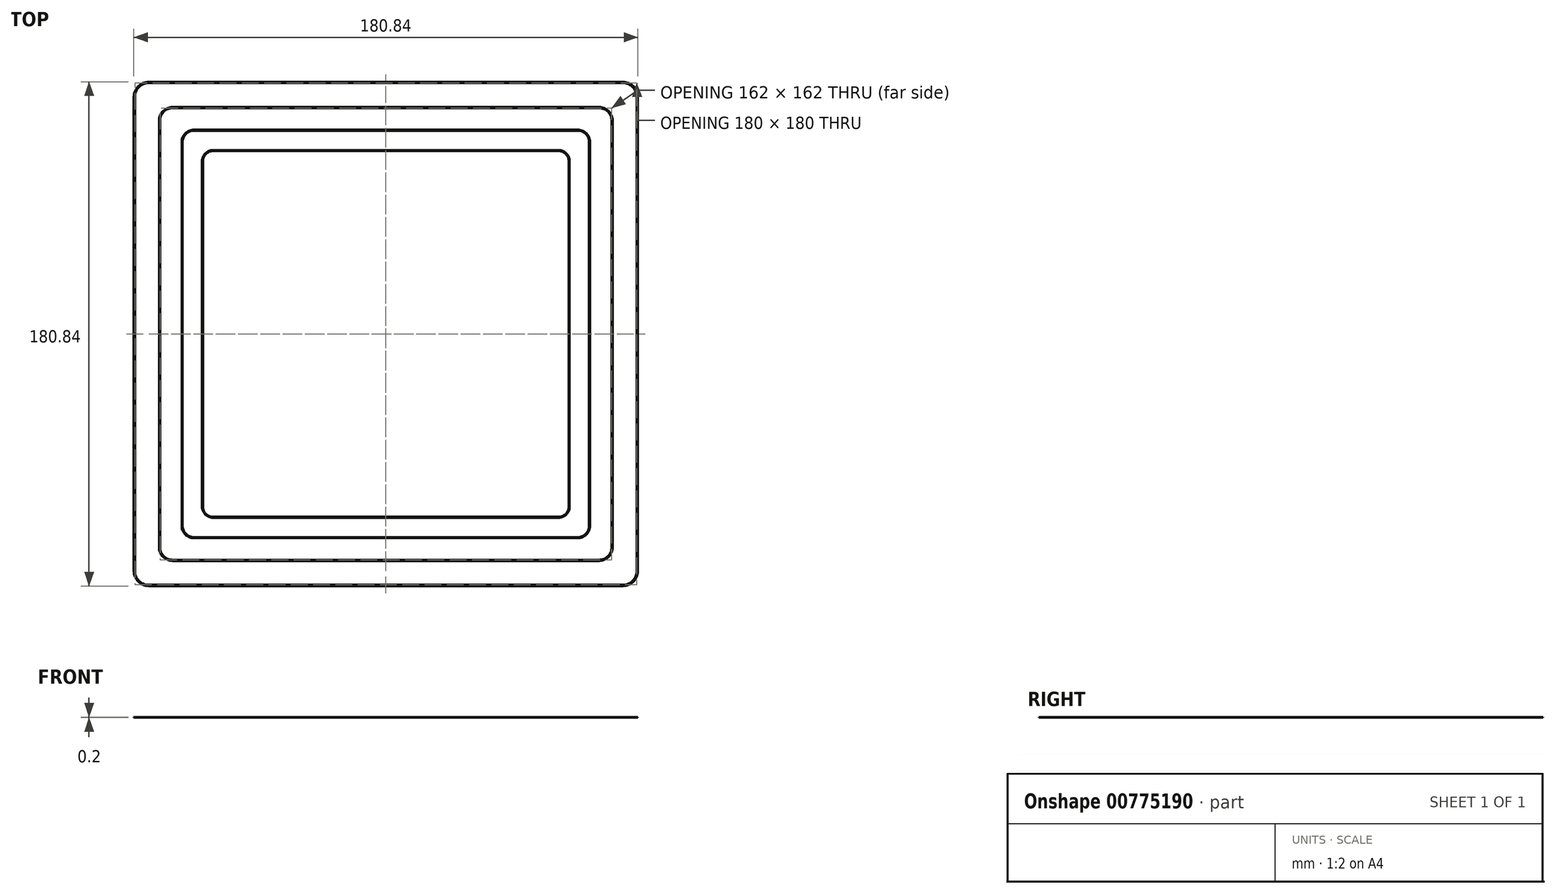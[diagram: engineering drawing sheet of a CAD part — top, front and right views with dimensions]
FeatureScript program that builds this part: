
annotation { "Feature Type Name" : "Feature", "Feature Type Description" : "" }
export const myFeature = defineFeature(function(context is Context, id is Id, definition is map)
    precondition{}
    {
        {
            var Q0;
            Q0=qCreatedBy(makeId("Top.planeOp"),FACE);
            var sketch = newSketch(context, id + "F0", { "sketchPlane" : qUnion([Q0])});
            skLineSegment(sketch, "E0.bottom", {"start": v(85, 90) * mm, "end": v(-85, 90) * mm});
            skLineSegment(sketch, "E0.top", {"start": v(85, -90) * mm, "end": v(-85, -90) * mm});
            skLineSegment(sketch, "E0.left", {"start": v(90, 85) * mm, "end": v(90, -85) * mm});
            skLineSegment(sketch, "E0.right", {"start": v(-90, 85) * mm, "end": v(-90, -85) * mm});
            skPoint(sketch, "E0.middle", {"position": v(0, 0) * mm});
            skPoint(sketch, "E1.visualSharp", {"position": v(-90, 90) * mm});
            skArc(sketch, "E1.filletArc", {"start": v(-85, 90) * mm, "mid": v(-88.54, 88.54) * mm, "end": v(-90, 85) * mm});
            skPoint(sketch, "E2.visualSharp", {"position": v(90, 90) * mm});
            skArc(sketch, "E2.filletArc", {"start": v(90, 85) * mm, "mid": v(88.54, 88.54) * mm, "end": v(85, 90) * mm});
            skPoint(sketch, "E3.visualSharp", {"position": v(90, -90) * mm});
            skArc(sketch, "E3.filletArc", {"start": v(85, -90) * mm, "mid": v(88.54, -88.54) * mm, "end": v(90, -85) * mm});
            skPoint(sketch, "E4.visualSharp", {"position": v(-90, -90) * mm});
            skArc(sketch, "E4.filletArc", {"start": v(-90, -85) * mm, "mid": v(-88.54, -88.54) * mm, "end": v(-85, -90) * mm});
            skArc(sketch, "E5.0", {"start": v(90.42, 85) * mm, "mid": v(88.83, 88.83) * mm, "end": v(85, 90.42) * mm});
            skLineSegment(sketch, "E5.1", {"start": v(90.42, 85) * mm, "end": v(90.42, -85) * mm});
            skLineSegment(sketch, "E5.2", {"start": v(85, 90.42) * mm, "end": v(-85, 90.42) * mm});
            skArc(sketch, "E5.3", {"start": v(85, -90.42) * mm, "mid": v(88.83, -88.83) * mm, "end": v(90.42, -85) * mm});
            skArc(sketch, "E5.4", {"start": v(-85, 90.42) * mm, "mid": v(-88.83, 88.83) * mm, "end": v(-90.42, 85) * mm});
            skLineSegment(sketch, "E5.5", {"start": v(-90.42, 85) * mm, "end": v(-90.42, -85) * mm});
            skArc(sketch, "E5.6", {"start": v(-90.42, -85) * mm, "mid": v(-88.83, -88.83) * mm, "end": v(-85, -90.42) * mm});
            skLineSegment(sketch, "E5.7", {"start": v(85, -90.42) * mm, "end": v(-85, -90.42) * mm});
            skSolve(sketch);
        }
        {
            var Q0;
            Q0 = qSketchRegion(id + "F0", true);
            extrude(context, id + "F1", {"entities" : qUnion([Q0]), "depth" : 0.2 * mm, "offsetDistance" : 25 * mm});
        }
        {
            var Q0;
            Q0=makeQuery(id+"F1.opExtrude","SWEPT_BODY",BODY,{"disambiguationData":[OSD([sQuery(id+"F0.wireOp",EDGE,"E0.bottom"),sQuery(id+"F0.wireOp",EDGE,"E0.top"),sQuery(id+"F0.wireOp",EDGE,"E0.left"),sQuery(id+"F0.wireOp",EDGE,"E0.right"),sQuery(id+"F0.wireOp",EDGE,"E1.filletArc"),sQuery(id+"F0.wireOp",EDGE,"E2.filletArc"),sQuery(id+"F0.wireOp",EDGE,"E3.filletArc"),sQuery(id+"F0.wireOp",EDGE,"E4.filletArc"),sQuery(id+"F0.wireOp",EDGE,"E5.0"),sQuery(id+"F0.wireOp",EDGE,"E5.1"),sQuery(id+"F0.wireOp",EDGE,"E5.2"),sQuery(id+"F0.wireOp",EDGE,"E5.3"),sQuery(id+"F0.wireOp",EDGE,"E5.4"),sQuery(id+"F0.wireOp",EDGE,"E5.5"),sQuery(id+"F0.wireOp",EDGE,"E5.6"),sQuery(id+"F0.wireOp",EDGE,"E5.7")])]});
            var Q1;
            Q1=qCreatedBy(makeId("Origin.pointOp"),VERTEX);
            transform(context, id + "F2", {"entities" : qUnion([Q0]), "transformType" : TransformType.SCALE_UNIFORMLY, "scale" : 0.9, "scalePoint" : qUnion([Q1]), "makeCopy" : true});
        }
        {
            var Q0;
            Q0=makeQuery(id+"F2.opPattern","COPY",BODY,{"derivedFrom":makeQuery(id+"F1.opExtrude","SWEPT_BODY",BODY,{"disambiguationData":[OSD([sQuery(id+"F0.wireOp",EDGE,"E0.bottom"),sQuery(id+"F0.wireOp",EDGE,"E0.top"),sQuery(id+"F0.wireOp",EDGE,"E0.left"),sQuery(id+"F0.wireOp",EDGE,"E0.right"),sQuery(id+"F0.wireOp",EDGE,"E1.filletArc"),sQuery(id+"F0.wireOp",EDGE,"E2.filletArc"),sQuery(id+"F0.wireOp",EDGE,"E3.filletArc"),sQuery(id+"F0.wireOp",EDGE,"E4.filletArc"),sQuery(id+"F0.wireOp",EDGE,"E5.0"),sQuery(id+"F0.wireOp",EDGE,"E5.1"),sQuery(id+"F0.wireOp",EDGE,"E5.2"),sQuery(id+"F0.wireOp",EDGE,"E5.3"),sQuery(id+"F0.wireOp",EDGE,"E5.4"),sQuery(id+"F0.wireOp",EDGE,"E5.5"),sQuery(id+"F0.wireOp",EDGE,"E5.6"),sQuery(id+"F0.wireOp",EDGE,"E5.7")])]}),"instanceName":"1"});
            var Q1;
            Q1=qCreatedBy(makeId("Origin.pointOp"),VERTEX);
            transform(context, id + "F3", {"entities" : qUnion([Q0]), "transformType" : TransformType.SCALE_UNIFORMLY, "scale" : 0.9, "scalePoint" : qUnion([Q1]), "makeCopy" : true});
        }
        {
            var Q0;
            Q0=makeQuery(id+"F3.opPattern","COPY",BODY,{"derivedFrom":makeQuery(id+"F2.opPattern","COPY",BODY,{"derivedFrom":makeQuery(id+"F1.opExtrude","SWEPT_BODY",BODY,{"disambiguationData":[OSD([sQuery(id+"F0.wireOp",EDGE,"E0.bottom"),sQuery(id+"F0.wireOp",EDGE,"E0.top"),sQuery(id+"F0.wireOp",EDGE,"E0.left"),sQuery(id+"F0.wireOp",EDGE,"E0.right"),sQuery(id+"F0.wireOp",EDGE,"E1.filletArc"),sQuery(id+"F0.wireOp",EDGE,"E2.filletArc"),sQuery(id+"F0.wireOp",EDGE,"E3.filletArc"),sQuery(id+"F0.wireOp",EDGE,"E4.filletArc"),sQuery(id+"F0.wireOp",EDGE,"E5.0"),sQuery(id+"F0.wireOp",EDGE,"E5.1"),sQuery(id+"F0.wireOp",EDGE,"E5.2"),sQuery(id+"F0.wireOp",EDGE,"E5.3"),sQuery(id+"F0.wireOp",EDGE,"E5.4"),sQuery(id+"F0.wireOp",EDGE,"E5.5"),sQuery(id+"F0.wireOp",EDGE,"E5.6"),sQuery(id+"F0.wireOp",EDGE,"E5.7")])]}),"instanceName":"1"}),"instanceName":"1"});
            var Q1;
            Q1=qCreatedBy(makeId("Origin.pointOp"),VERTEX);
            transform(context, id + "F4", {"entities" : qUnion([Q0]), "transformType" : TransformType.SCALE_UNIFORMLY, "scale" : 0.9, "scalePoint" : qUnion([Q1]), "makeCopy" : true});
        }
    });
